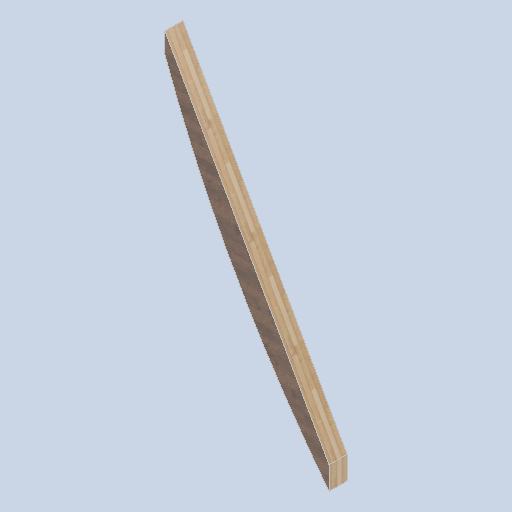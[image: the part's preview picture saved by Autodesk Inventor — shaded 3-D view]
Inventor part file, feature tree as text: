
AUTODESK INVENTOR PART (.ipt)
format: ipt  version: 2024.2 (Build 282272000, 272)  size: 121,856 bytes
history: native  units: in
note: dims shown in document units (in); Inventor stores cm internally (conversion verified against a paired STEP export)
features: other x3, sketch x1
ambient origin geometry x8: Origin, YZ Plane, XZ Plane, XY Plane, X Axis, Y Axis, Z Axis, Center Point
bodies: Body1 (feature_tree)
feature tree (4):
  other  "side_curve_beam_04_MIR.ipt"
  other  "Solid2::side_curve_beam_04_MIR.ipt"
  other  "TaggingFeature1"
  sketch  "Sketch1"  dims[d0=0.3937in]
